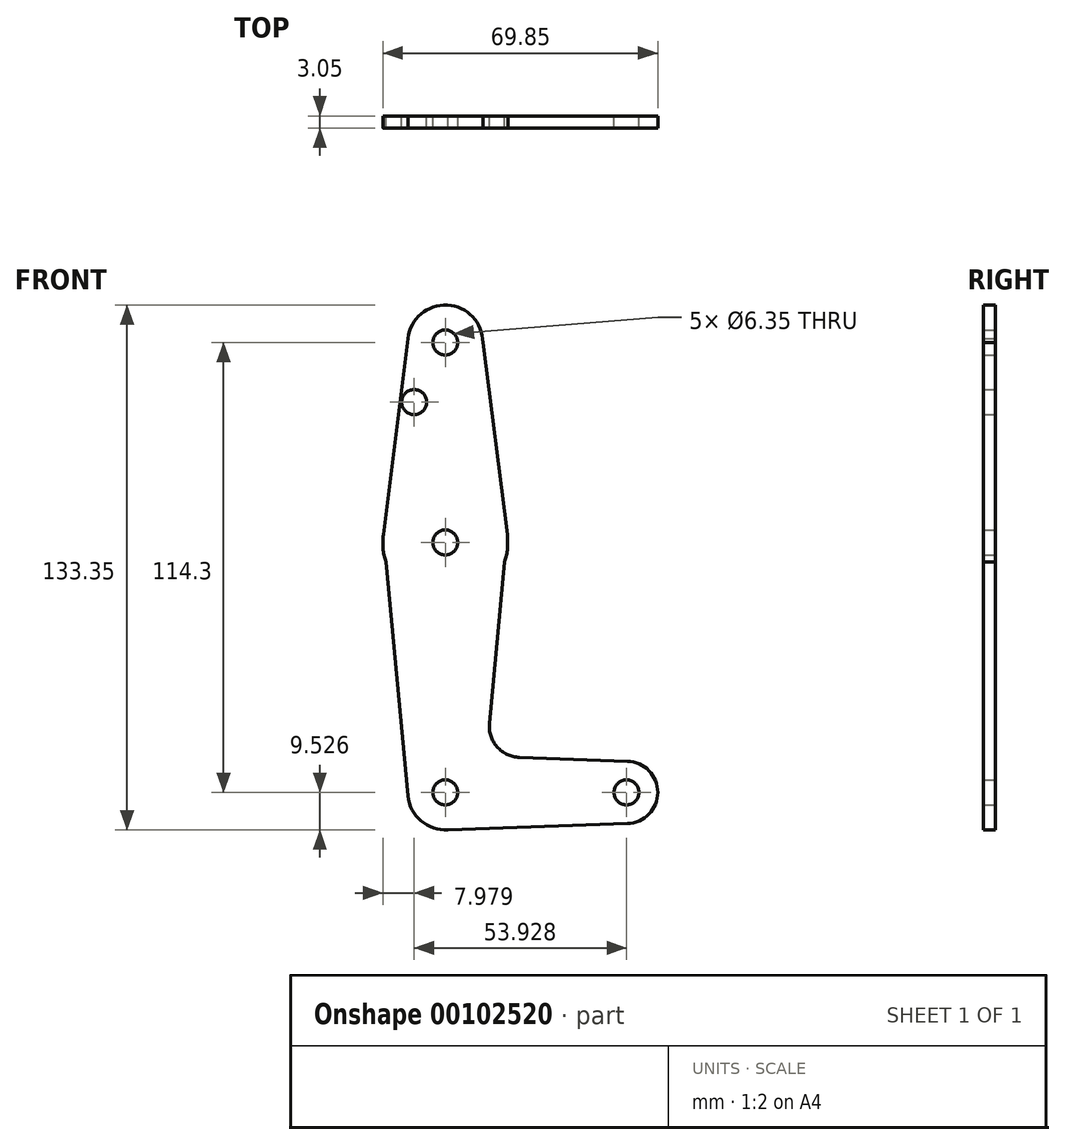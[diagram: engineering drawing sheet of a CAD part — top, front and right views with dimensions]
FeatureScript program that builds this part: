
annotation { "Feature Type Name" : "Feature", "Feature Type Description" : "" }
export const myFeature = defineFeature(function(context is Context, id is Id, definition is map)
    precondition{}
    {
        {
            var Q0;
            Q0=qCreatedBy(makeId("Front.planeOp"),FACE);
            var sketch = newSketch(context, id + "F0", { "sketchPlane" : qUnion([Q0])});
            skLineSegment(sketch, "E0", {"start": v(0, 92.8) * mm, "end": v(0, -79.67) * mm});
            skCircle(sketch, "E1", {"center": v(0, 42) * mm, "radius": 15.88 * mm});
            skCircle(sketch, "E2", {"center": v(0, 92.8) * mm, "radius": 9.53 * mm});
            skCircle(sketch, "E3", {"center": v(0, -21.5) * mm, "radius": 9.53 * mm});
            skCircle(sketch, "E4", {"center": v(46.04, -21.5) * mm, "radius": 7.94 * mm});
            skLineSegment(sketch, "E5", {"start": v(0, -21.5) * mm, "end": v(46.04, -21.5) * mm});
            skLineSegment(sketch, "E6", {"start": v(-9.43, 94.12) * mm, "end": v(-15.75, 43.98) * mm});
            skLineSegment(sketch, "E7", {"start": v(-15.75, 43.98) * mm, "end": v(-9.48, -22.4) * mm});
            skLineSegment(sketch, "E8", {"start": v(9.53, 92.8) * mm, "end": v(15.75, 43.98) * mm});
            skLineSegment(sketch, "E9", {"start": v(15.75, 43.98) * mm, "end": v(11.23, -3.94) * mm});
            skLineSegment(sketch, "E10", {"start": v(18.87, -12.63) * mm, "end": v(46.31, -13.57) * mm});
            skLineSegment(sketch, "E11", {"start": v(0, -31.03) * mm, "end": v(46.31, -29.44) * mm});
            skCircle(sketch, "E12", {"center": v(0, 92.8) * mm, "radius": 3.18 * mm});
            skCircle(sketch, "E13", {"center": v(-7.9, 77.66) * mm, "radius": 3.18 * mm});
            skCircle(sketch, "E14", {"center": v(0, 42) * mm, "radius": 3.18 * mm});
            skCircle(sketch, "E15", {"center": v(0, -21.5) * mm, "radius": 3.18 * mm});
            skCircle(sketch, "E16", {"center": v(46.04, -21.5) * mm, "radius": 3.18 * mm});
            skPoint(sketch, "E17.newPointA", {"position": v(9.48, -22.4) * mm});
            skArc(sketch, "E17.filletArc", {"start": v(11.23, -3.94) * mm, "mid": v(13.17, -9.93) * mm, "end": v(18.87, -12.63) * mm});
            skSolve(sketch);
        }
        {
            var Q0;
            Q0 = qSketchRegion(id + "F0", true);
            var Q1;
            {var subQ0=sQuery(id+"F0.wireOp",EDGE,"E3");var subQ1=sQuery(id+"F0.wireOp",EDGE,"E0");var subQ2=makeQuery(id+"F0.imprint","INTERSECT",VERTEX,{"derivedFrom":[subQ1,subQ0]});Q1=makeQuery(id+"F0.imprint","IMPRINT",FACE,{"disambiguationData":[TD([[makeQuery(id+"F0.imprint","IMPRINT",EDGE,{"disambiguationData":[TD([[subQ2,-1.0]])],"derivedFrom":subQ1}),1.0]])]});}
            extrude(context, id + "F1", {"entities" : qUnion([Q0, Q1]), "depth" : 3.05 * mm});
        }
    });
